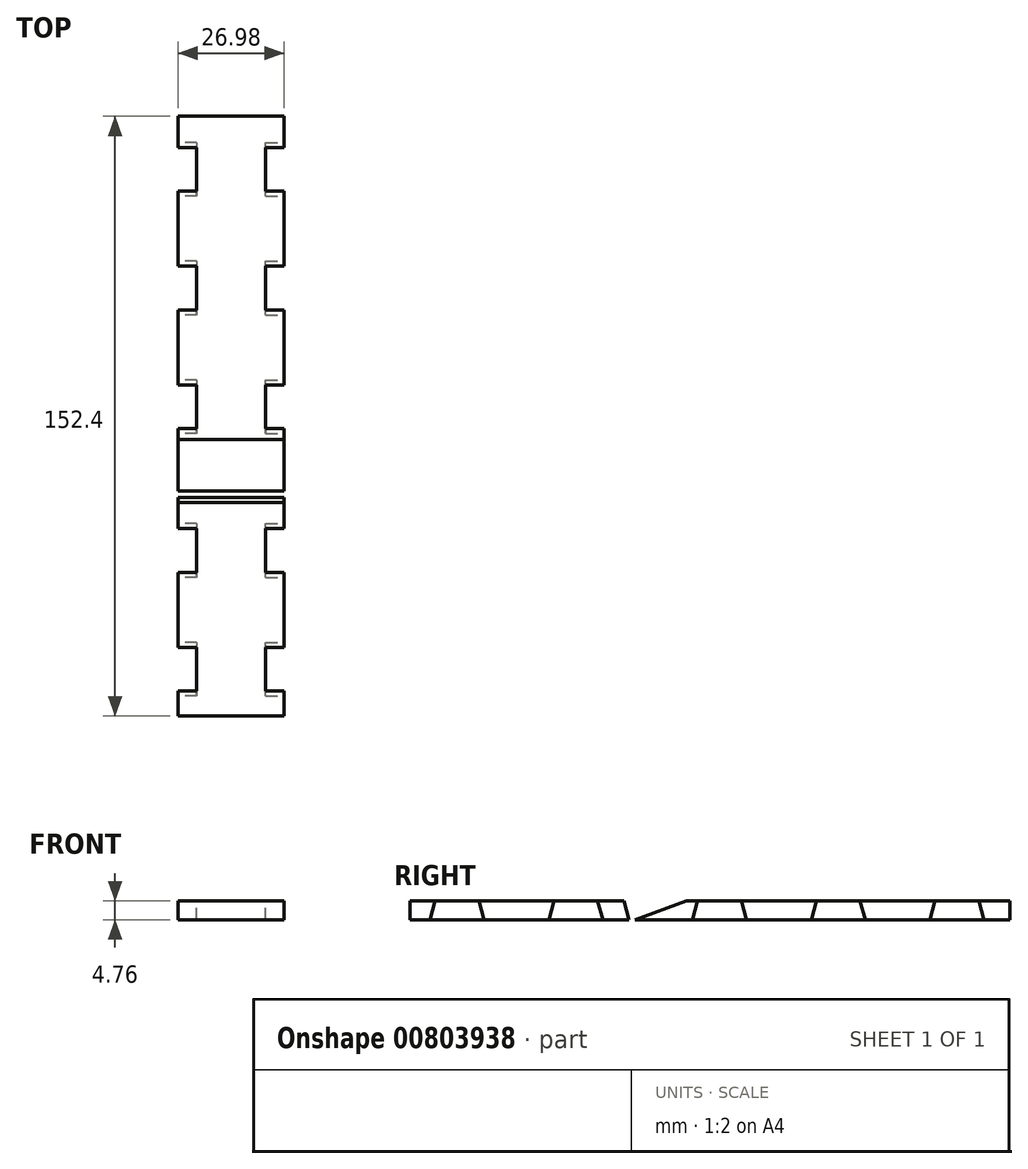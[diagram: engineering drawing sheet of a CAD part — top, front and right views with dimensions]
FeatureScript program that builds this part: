
annotation { "Feature Type Name" : "Feature", "Feature Type Description" : "" }
export const myFeature = defineFeature(function(context is Context, id is Id, definition is map)
    precondition{}
    {
        {
            var Q0;
            Q0=qCreatedBy(makeId("Right.planeOp"),FACE);
            var sketch = newSketch(context, id + "F0", { "sketchPlane" : qUnion([Q0])});
            skLineSegment(sketch, "E0", {"start": v(0, 57.61) * mm, "end": v(0, -31.84) * mm, "construction": true});
            skLineSegment(sketch, "E1.bottom", {"start": v(-76.2, 0) * mm, "end": v(76.2, 0) * mm});
            skLineSegment(sketch, "E1.top", {"start": v(-76.2, -4.76) * mm, "end": v(76.2, -4.76) * mm});
            skLineSegment(sketch, "E1.left", {"start": v(-76.2, 0) * mm, "end": v(-76.2, -4.76) * mm});
            skLineSegment(sketch, "E1.right", {"start": v(76.2, 0) * mm, "end": v(76.2, -4.76) * mm});
            skSolve(sketch);
        }
        {
            var Q0;
            Q0=makeQuery(id+"F0.imprint","IMPRINT",FACE,{"disambiguationData":[TD([[makeQuery(id+"F0.imprint","IMPRINT",EDGE,{"derivedFrom":sQuery(id+"F0.wireOp",EDGE,"E1.bottom")}),-1.0]])]});
            extrude(context, id + "F1", {"entities" : qUnion([Q0]), "endBound" : BoundingType.SYMMETRIC, "depth" : 26.99 * mm, "offsetDistance" : 25.4 * mm});
        }
        {
            var Q0;
            Q0=makeQuery(id+"F1.opExtrude","CAP_FACE",FACE,{"disambiguationData":[OSD([sQuery(id+"F0.wireOp",EDGE,"E1.bottom"),sQuery(id+"F0.wireOp",EDGE,"E1.top"),sQuery(id+"F0.wireOp",EDGE,"E1.left"),sQuery(id+"F0.wireOp",EDGE,"E1.right")])],"isStart":false});
            var sketch = newSketch(context, id + "F2", { "sketchPlane" : qUnion([Q0])});
            skLineSegment(sketch, "E2.0.0", {"start": v(-76.2, 0) * mm, "end": v(-76.2, -4.76) * mm});
            skLineSegment(sketch, "E2.0.1", {"start": v(-76.2, -4.76) * mm, "end": v(76.2, -4.76) * mm});
            skLineSegment(sketch, "E2.0.2", {"start": v(76.2, -4.76) * mm, "end": v(76.2, 0) * mm});
            skLineSegment(sketch, "E2.0.3", {"start": v(76.2, 0) * mm, "end": v(-76.2, 0) * mm});
            skLineSegment(sketch, "E3", {"start": v(-71.13, -4.76) * mm, "end": v(-69.85, 0) * mm});
            skLineSegment(sketch, "E4", {"start": v(-69.85, 0) * mm, "end": v(-58.74, 0) * mm});
            skLineSegment(sketch, "E5", {"start": v(-58.74, 0) * mm, "end": v(-57.46, -4.76) * mm});
            skLineSegment(sketch, "E6", {"start": v(-57.46, -4.76) * mm, "end": v(-40.96, -4.76) * mm});
            skLineSegment(sketch, "E7", {"start": v(-40.96, -4.76) * mm, "end": v(-39.69, 0) * mm});
            skLineSegment(sketch, "E8", {"start": v(-39.69, 0) * mm, "end": v(-28.57, 0) * mm});
            skLineSegment(sketch, "E9", {"start": v(-28.57, 0) * mm, "end": v(-27.3, -4.76) * mm});
            skLineSegment(sketch, "E10", {"start": v(-3.17, 0) * mm, "end": v(-4.45, -4.76) * mm});
            skLineSegment(sketch, "E11", {"start": v(7.94, 0) * mm, "end": v(9.21, -4.76) * mm});
            skLineSegment(sketch, "E12", {"start": v(9.21, -4.76) * mm, "end": v(25.71, -4.76) * mm});
            skLineSegment(sketch, "E13", {"start": v(25.71, -4.76) * mm, "end": v(26.99, 0) * mm});
            skLineSegment(sketch, "E14", {"start": v(26.99, 0) * mm, "end": v(38.1, 0) * mm});
            skLineSegment(sketch, "E15", {"start": v(38.1, 0) * mm, "end": v(39.38, -4.76) * mm});
            skLineSegment(sketch, "E16", {"start": v(39.38, -4.76) * mm, "end": v(55.87, -4.76) * mm});
            skLineSegment(sketch, "E17", {"start": v(55.87, -4.76) * mm, "end": v(57.15, 0) * mm});
            skLineSegment(sketch, "E18", {"start": v(57.15, 0) * mm, "end": v(68.26, 0) * mm});
            skLineSegment(sketch, "E19", {"start": v(68.26, 0) * mm, "end": v(69.54, -4.76) * mm});
            skSolve(sketch);
        }
        {
            var Q0;
            {var subQ0=sQuery(id+"F2.wireOp",EDGE,"E3");Q0=makeQuery(id+"F2.imprint","IMPRINT",FACE,{"disambiguationData":[TD([[makeQuery(id+"F2.imprint","IMPRINT",EDGE,{"derivedFrom":subQ0}),-1.0]])]});}
            var Q1;
            {var subQ0=sQuery(id+"F2.wireOp",EDGE,"E7");Q1=makeQuery(id+"F2.imprint","IMPRINT",FACE,{"disambiguationData":[TD([[makeQuery(id+"F2.imprint","IMPRINT",EDGE,{"derivedFrom":subQ0}),-1.0]])]});}
            var Q2;
            {var subQ0=sQuery(id+"F2.wireOp",EDGE,"E10");Q2=makeQuery(id+"F2.imprint","IMPRINT",FACE,{"disambiguationData":[TD([[makeQuery(id+"F2.imprint","IMPRINT",EDGE,{"derivedFrom":subQ0}),1.0]])]});}
            var Q3;
            {var subQ0=sQuery(id+"F2.wireOp",EDGE,"E13");Q3=makeQuery(id+"F2.imprint","IMPRINT",FACE,{"disambiguationData":[TD([[makeQuery(id+"F2.imprint","IMPRINT",EDGE,{"derivedFrom":subQ0}),-1.0]])]});}
            var Q4;
            {var subQ0=sQuery(id+"F2.wireOp",EDGE,"E17");Q4=makeQuery(id+"F2.imprint","IMPRINT",FACE,{"disambiguationData":[TD([[makeQuery(id+"F2.imprint","IMPRINT",EDGE,{"derivedFrom":subQ0}),-1.0]])]});}
            extrude(context, id + "F3", {"entities" : qUnion([Q0, Q1, Q2, Q3, Q4]), "operationType" : NewBodyOperationType.REMOVE, "oppositeDirection" : true, "depth" : 4.76 * mm, "offsetDistance" : 25.4 * mm});
        }
        {
            var Q0;
            Q0=makeQuery(id+"F1.opExtrude","CAP_FACE",FACE,{"disambiguationData":[OSD([sQuery(id+"F0.wireOp",EDGE,"E1.bottom"),sQuery(id+"F0.wireOp",EDGE,"E1.top"),sQuery(id+"F0.wireOp",EDGE,"E1.left"),sQuery(id+"F0.wireOp",EDGE,"E1.right")])],"isStart":true});
            var sketch = newSketch(context, id + "F4", { "sketchPlane" : qUnion([Q0])});
            skLineSegment(sketch, "E20.0.0", {"start": v(57.46, -4.76) * mm, "end": v(58.74, 0) * mm});
            skLineSegment(sketch, "E20.0.1", {"start": v(58.74, 0) * mm, "end": v(69.85, 0) * mm});
            skLineSegment(sketch, "E20.0.2", {"start": v(69.85, 0) * mm, "end": v(71.13, -4.76) * mm});
            skLineSegment(sketch, "E20.0.3", {"start": v(71.13, -4.76) * mm, "end": v(57.46, -4.76) * mm});
            skLineSegment(sketch, "E21.0.0", {"start": v(27.3, -4.76) * mm, "end": v(28.57, 0) * mm});
            skLineSegment(sketch, "E21.0.1", {"start": v(28.57, 0) * mm, "end": v(39.69, 0) * mm});
            skLineSegment(sketch, "E21.0.2", {"start": v(39.69, 0) * mm, "end": v(40.96, -4.76) * mm});
            skLineSegment(sketch, "E21.0.3", {"start": v(40.96, -4.76) * mm, "end": v(27.3, -4.76) * mm});
            skLineSegment(sketch, "E22.0.0", {"start": v(-9.21, -4.76) * mm, "end": v(-7.94, 0) * mm});
            skLineSegment(sketch, "E22.0.1", {"start": v(-7.94, 0) * mm, "end": v(3.17, 0) * mm});
            skLineSegment(sketch, "E22.0.2", {"start": v(3.17, 0) * mm, "end": v(4.45, -4.76) * mm});
            skLineSegment(sketch, "E22.0.3", {"start": v(4.45, -4.76) * mm, "end": v(-9.21, -4.76) * mm});
            skLineSegment(sketch, "E23.0", {"start": v(-25.71, -4.76) * mm, "end": v(-39.38, -4.76) * mm});
            skLineSegment(sketch, "E24.0.0", {"start": v(-39.38, -4.76) * mm, "end": v(-38.1, 0) * mm});
            skLineSegment(sketch, "E24.0.1", {"start": v(-38.1, 0) * mm, "end": v(-26.99, 0) * mm});
            skLineSegment(sketch, "E24.0.2", {"start": v(-26.99, 0) * mm, "end": v(-25.71, -4.76) * mm});
            skLineSegment(sketch, "E25.0.0", {"start": v(-69.54, -4.76) * mm, "end": v(-68.26, 0) * mm});
            skLineSegment(sketch, "E25.0.1", {"start": v(-68.26, 0) * mm, "end": v(-57.15, 0) * mm});
            skLineSegment(sketch, "E25.0.2", {"start": v(-57.15, 0) * mm, "end": v(-55.87, -4.76) * mm});
            skLineSegment(sketch, "E25.0.3", {"start": v(-55.87, -4.76) * mm, "end": v(-69.54, -4.76) * mm});
            skSolve(sketch);
        }
        {
            var Q0;
            Q0=makeQuery(id+"F4.imprint","IMPRINT",FACE,{"disambiguationData":[TD([[makeQuery(id+"F4.imprint","IMPRINT",EDGE,{"derivedFrom":sQuery(id+"F4.wireOp",EDGE,"E25.0.0")}),-1.0]])]});
            var Q1;
            Q1=makeQuery(id+"F4.imprint","IMPRINT",FACE,{"disambiguationData":[TD([[makeQuery(id+"F4.imprint","IMPRINT",EDGE,{"derivedFrom":sQuery(id+"F4.wireOp",EDGE,"E24.0.0")}),-1.0]])]});
            var Q2;
            Q2=makeQuery(id+"F4.imprint","IMPRINT",FACE,{"disambiguationData":[TD([[makeQuery(id+"F4.imprint","IMPRINT",EDGE,{"derivedFrom":sQuery(id+"F4.wireOp",EDGE,"E22.0.0")}),-1.0]])]});
            var Q3;
            Q3=makeQuery(id+"F4.imprint","IMPRINT",FACE,{"disambiguationData":[TD([[makeQuery(id+"F4.imprint","IMPRINT",EDGE,{"derivedFrom":sQuery(id+"F4.wireOp",EDGE,"E21.0.0")}),-1.0]])]});
            var Q4;
            Q4=makeQuery(id+"F4.imprint","IMPRINT",FACE,{"disambiguationData":[TD([[makeQuery(id+"F4.imprint","IMPRINT",EDGE,{"derivedFrom":sQuery(id+"F4.wireOp",EDGE,"E20.0.0")}),-1.0]])]});
            extrude(context, id + "F5", {"entities" : qUnion([Q0, Q1, Q2, Q3, Q4]), "operationType" : NewBodyOperationType.REMOVE, "oppositeDirection" : true, "depth" : 4.76 * mm, "offsetDistance" : 25.4 * mm});
        }
        {
            var Q0;
            {var subQ0=sQuery(id+"F0.wireOp",EDGE,"E1.bottom");var subQ1=sQuery(id+"F0.wireOp",EDGE,"E1.top");Q0=makeQuery(id+"F3.boolean.opBoolean","SPLIT",FACE,{"disambiguationData":[TD([makeQuery(id+"F3.opExtrude","SWEPT_FACE",FACE,{"disambiguationData":[OSD([sQuery(id+"F2.wireOp",EDGE,"E9")])]})])],"derivedFrom":makeQuery(id+"F1.opExtrude","CAP_FACE",FACE,{"disambiguationData":[OSD([subQ0,subQ1,sQuery(id+"F0.wireOp",EDGE,"E1.left"),sQuery(id+"F0.wireOp",EDGE,"E1.right")])],"isStart":false})});}
            var sketch = newSketch(context, id + "F6", { "sketchPlane" : qUnion([Q0])});
            skLineSegment(sketch, "E26.0.0", {"start": v(-3.17, 0) * mm, "end": v(-28.57, 0) * mm});
            skLineSegment(sketch, "E26.0.1", {"start": v(-28.57, 0) * mm, "end": v(-27.3, -4.76) * mm});
            skLineSegment(sketch, "E26.0.2", {"start": v(-27.3, -4.76) * mm, "end": v(-4.45, -4.76) * mm});
            skLineSegment(sketch, "E26.0.3", {"start": v(-4.45, -4.76) * mm, "end": v(-3.17, 0) * mm});
            skPoint(sketch, "E27.0", {"position": v(-76.2, -2.38) * mm});
            skPoint(sketch, "E28.0", {"position": v(76.2, -2.38) * mm});
            skLineSegment(sketch, "E29", {"start": v(-21.91, 0) * mm, "end": v(-20.64, -4.76) * mm});
            skLineSegment(sketch, "E30", {"start": v(-19.05, -4.76) * mm, "end": v(-5.97, 0) * mm});
            skSolve(sketch);
        }
        {
            var Q0;
            {var subQ0=sQuery(id+"F6.wireOp",EDGE,"E29");Q0=makeQuery(id+"F6.imprint","IMPRINT",FACE,{"disambiguationData":[TD([[makeQuery(id+"F6.imprint","IMPRINT",EDGE,{"derivedFrom":subQ0}),1.0]])]});}
            extrude(context, id + "F7", {"entities" : qUnion([Q0]), "operationType" : NewBodyOperationType.REMOVE, "endBound" : BoundingType.THROUGH_ALL, "oppositeDirection" : true, "depth" : 25.4 * mm, "offsetDistance" : 25.4 * mm});
        }
    });
